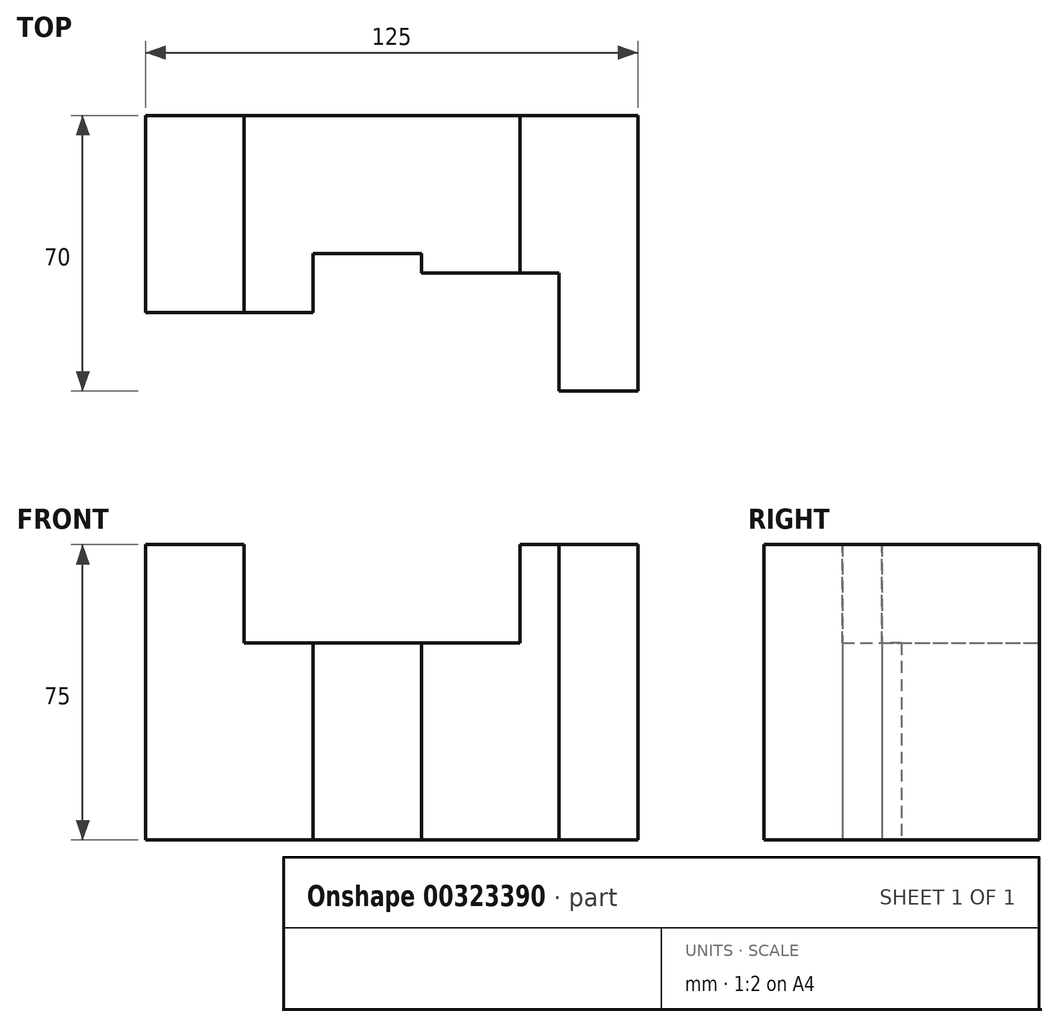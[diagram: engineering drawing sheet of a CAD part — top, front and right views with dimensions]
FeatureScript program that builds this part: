
annotation { "Feature Type Name" : "Feature", "Feature Type Description" : "" }
export const myFeature = defineFeature(function(context is Context, id is Id, definition is map)
    precondition{}
    {
        {
            var Q0;
            Q0=qCreatedBy(makeId("Top.planeOp"),FACE);
            var sketch = newSketch(context, id + "F0", { "sketchPlane" : qUnion([Q0])});
            skLineSegment(sketch, "E0", {"start": v(0, 0) * mm, "end": v(42.5, 0) * mm});
            skLineSegment(sketch, "E1", {"start": v(42.5, 0) * mm, "end": v(42.5, 15) * mm});
            skLineSegment(sketch, "E2", {"start": v(42.5, 15) * mm, "end": v(70, 15) * mm});
            skLineSegment(sketch, "E3", {"start": v(70, 15) * mm, "end": v(70, 10) * mm});
            skLineSegment(sketch, "E4", {"start": v(70, 10) * mm, "end": v(105, 10) * mm});
            skLineSegment(sketch, "E5", {"start": v(105, -20) * mm, "end": v(125, -20) * mm});
            skLineSegment(sketch, "E6", {"start": v(125, -20) * mm, "end": v(125, 50) * mm});
            skLineSegment(sketch, "E7", {"start": v(125, 50) * mm, "end": v(0, 50) * mm});
            skLineSegment(sketch, "E8", {"start": v(0, 50) * mm, "end": v(0, 0) * mm});
            skLineSegment(sketch, "E9", {"start": v(105, 10) * mm, "end": v(105, -20) * mm});
            skSolve(sketch);
        }
        {
            var Q0;
            Q0 = qSketchRegion(id + "F0", true);
            extrude(context, id + "F1", {"entities" : qUnion([Q0]), "depth" : 75 * mm});
        }
        {
            var Q0;
            Q0=makeQuery(id+"F1.opExtrude","CAP_FACE",FACE,{"disambiguationData":[OSD([sQuery(id+"F0.wireOp",EDGE,"E0"),sQuery(id+"F0.wireOp",EDGE,"E1"),sQuery(id+"F0.wireOp",EDGE,"E2"),sQuery(id+"F0.wireOp",EDGE,"E3"),sQuery(id+"F0.wireOp",EDGE,"E4"),sQuery(id+"F0.wireOp",EDGE,"E5"),sQuery(id+"F0.wireOp",EDGE,"E6"),sQuery(id+"F0.wireOp",EDGE,"E7"),sQuery(id+"F0.wireOp",EDGE,"E8"),sQuery(id+"F0.wireOp",EDGE,"E9")])],"isStart":false});
            var sketch = newSketch(context, id + "F2", { "sketchPlane" : qUnion([Q0])});
            skLineSegment(sketch, "E10.0.0", {"start": v(125, -20) * mm, "end": v(125, 50) * mm});
            skLineSegment(sketch, "E10.0.1", {"start": v(125, 50) * mm, "end": v(0, 50) * mm});
            skLineSegment(sketch, "E10.0.2", {"start": v(0, 50) * mm, "end": v(0, 0) * mm});
            skLineSegment(sketch, "E10.0.3", {"start": v(0, 0) * mm, "end": v(42.5, 0) * mm});
            skLineSegment(sketch, "E10.0.4", {"start": v(42.5, 0) * mm, "end": v(42.5, 15) * mm});
            skLineSegment(sketch, "E10.0.5", {"start": v(42.5, 15) * mm, "end": v(70, 15) * mm});
            skLineSegment(sketch, "E10.0.6", {"start": v(70, 15) * mm, "end": v(70, 10) * mm});
            skLineSegment(sketch, "E10.0.7", {"start": v(70, 10) * mm, "end": v(105, 10) * mm});
            skLineSegment(sketch, "E10.0.8", {"start": v(105, 10) * mm, "end": v(105, -20) * mm});
            skLineSegment(sketch, "E10.0.9", {"start": v(105, -20) * mm, "end": v(125, -20) * mm});
            skLineSegment(sketch, "E11", {"start": v(25, 0) * mm, "end": v(25, 50) * mm});
            skLineSegment(sketch, "E12", {"start": v(25, 0) * mm, "end": v(42.5, 0) * mm});
            skLineSegment(sketch, "E13", {"start": v(70, 10) * mm, "end": v(95, 10) * mm});
            skLineSegment(sketch, "E14", {"start": v(95, 10) * mm, "end": v(95, 50) * mm});
            skLineSegment(sketch, "E15", {"start": v(95, 50) * mm, "end": v(25, 50) * mm});
            skSolve(sketch);
        }
        {
            var Q0;
            Q0=makeQuery(id+"F2.imprint","IMPRINT",FACE,{"disambiguationData":[TD([[makeQuery(id+"F2.imprint","IMPRINT",EDGE,{"derivedFrom":sQuery(id+"F2.wireOp",EDGE,"E10.0.4")}),1.0]])]});
            extrude(context, id + "F3", {"entities" : qUnion([Q0]), "operationType" : NewBodyOperationType.REMOVE, "oppositeDirection" : true, "depth" : 25 * mm});
        }
    });
